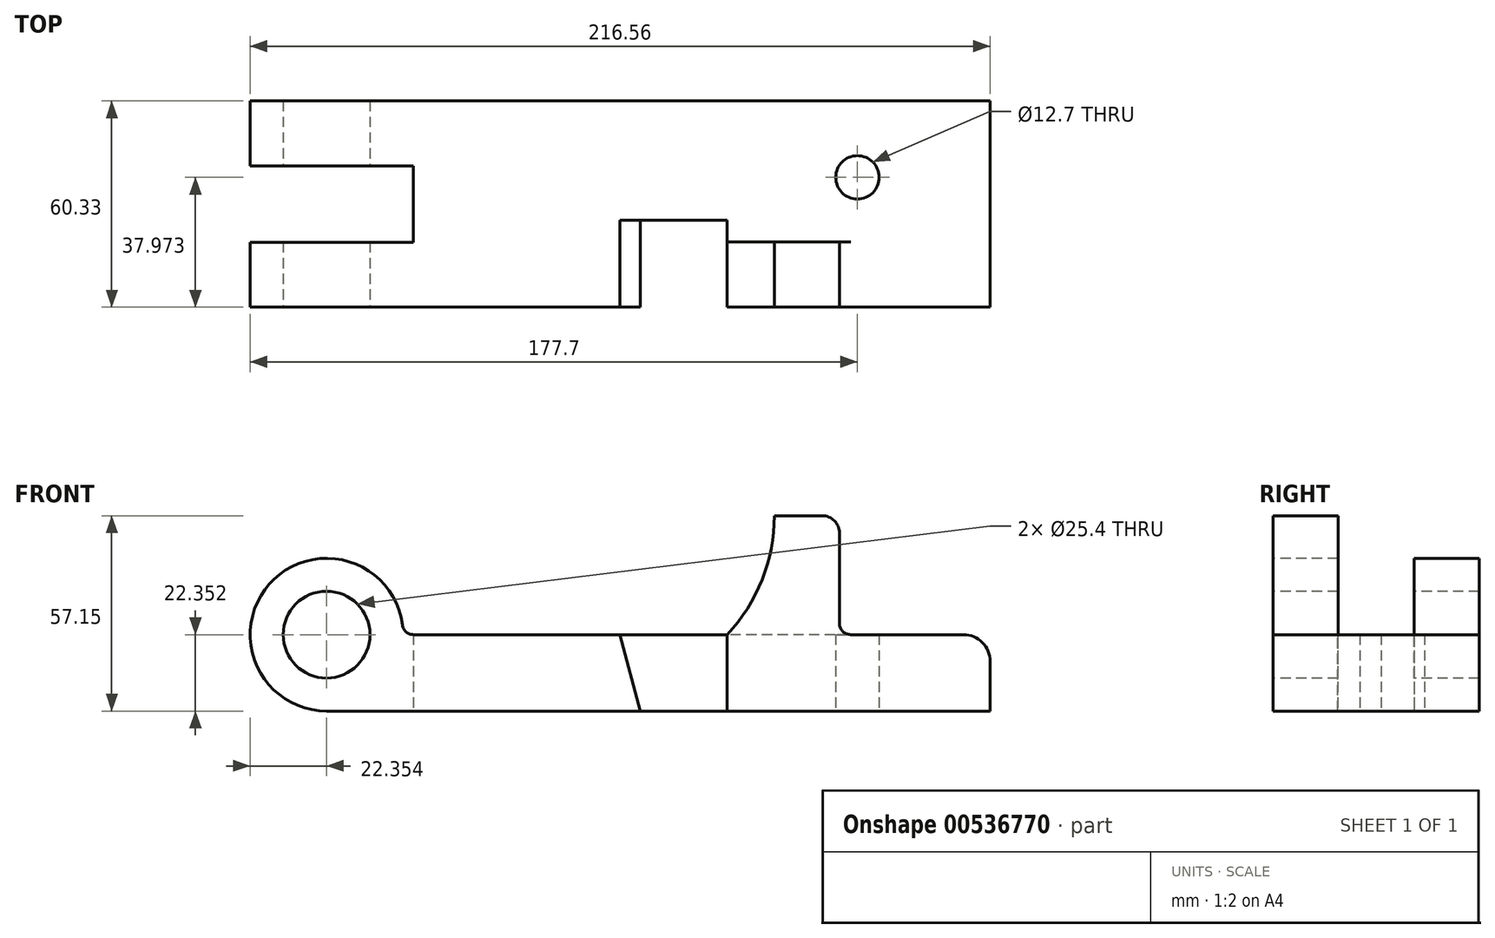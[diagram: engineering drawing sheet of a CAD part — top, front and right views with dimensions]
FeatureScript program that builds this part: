
annotation { "Feature Type Name" : "Feature", "Feature Type Description" : "" }
export const myFeature = defineFeature(function(context is Context, id is Id, definition is map)
    precondition{}
    {
        {
            var Q0;
            Q0=qCreatedBy(makeId("Front.planeOp"),FACE);
            var sketch = newSketch(context, id + "F0", { "sketchPlane" : qUnion([Q0])});
            skLineSegment(sketch, "E0", {"start": v(0, 0) * mm, "end": v(-91.85, 0) * mm});
            skLineSegment(sketch, "E1", {"start": v(0, 0) * mm, "end": v(102.36, 0) * mm});
            skLineSegment(sketch, "E2", {"start": v(102.36, 0) * mm, "end": v(102.36, 14.48) * mm});
            skLineSegment(sketch, "E3", {"start": v(61.54, 22.35) * mm, "end": v(94.49, 22.35) * mm});
            skLineSegment(sketch, "E4", {"start": v(58.24, 25.65) * mm, "end": v(58.24, 52.07) * mm});
            skLineSegment(sketch, "E5", {"start": v(53.16, 57.15) * mm, "end": v(39.2, 57.15) * mm});
            skLineSegment(sketch, "E6", {"start": v(39.2, 57.15) * mm, "end": v(39.2, 22.35) * mm, "construction": true});
            skLineSegment(sketch, "E7", {"start": v(39.2, 22.35) * mm, "end": v(25.4, 22.35) * mm});
            skLineSegment(sketch, "E8", {"start": v(25.4, 22.35) * mm, "end": v(-6, 22.35) * mm});
            skLineSegment(sketch, "E9", {"start": v(-6, 22.35) * mm, "end": v(-66.4, 22.35) * mm});
            skCircle(sketch, "E10", {"center": v(-91.85, 22.35) * mm, "radius": 12.7 * mm});
            skArc(sketch, "E11", {"start": v(102.36, 14.48) * mm, "mid": v(100.06, 20.05) * mm, "end": v(94.49, 22.35) * mm});
            skPoint(sketch, "E12", {"position": v(102.36, 22.35) * mm});
            skArc(sketch, "E13", {"start": v(-69.5, 22.35) * mm, "mid": v(-69.54, 23.8) * mm, "end": v(-69.68, 25.23) * mm, "construction": true});
            skArc(sketch, "E14", {"start": v(-91.85, 0) * mm, "mid": v(-76.04, 6.55) * mm, "end": v(-69.5, 22.35) * mm, "construction": true});
            skLineSegment(sketch, "E15", {"start": v(-6, 22.35) * mm, "end": v(0, 0) * mm});
            skLineSegment(sketch, "E16", {"start": v(25.4, 22.35) * mm, "end": v(25.4, 0) * mm});
            skArc(sketch, "E17", {"start": v(25.4, 22.35) * mm, "mid": v(35.62, 38.43) * mm, "end": v(39.2, 57.15) * mm});
            skArc(sketch, "E18", {"start": v(-69.68, 25.23) * mm, "mid": v(-68.59, 23.17) * mm, "end": v(-66.4, 22.35) * mm});
            skLineSegment(sketch, "E19", {"start": v(-66.4, 22.35) * mm, "end": v(-69.5, 22.35) * mm, "construction": true});
            skArc(sketch, "E20", {"start": v(-69.68, 25.23) * mm, "mid": v(-108.64, 37.1) * mm, "end": v(-91.85, 0) * mm});
            skArc(sketch, "E21", {"start": v(58.24, 52.07) * mm, "mid": v(56.75, 55.66) * mm, "end": v(53.16, 57.15) * mm});
            skArc(sketch, "E22", {"start": v(58.24, 25.65) * mm, "mid": v(59.2, 23.32) * mm, "end": v(61.54, 22.35) * mm});
            skPoint(sketch, "E23.orphan", {"position": v(58.24, 22.35) * mm});
            skPoint(sketch, "E24.orphan", {"position": v(58.24, 57.15) * mm});
            skLineSegment(sketch, "E25", {"start": v(61.54, 22.35) * mm, "end": v(58.24, 22.35) * mm});
            skLineSegment(sketch, "E26", {"start": v(58.24, 22.35) * mm, "end": v(39.2, 22.35) * mm});
            skSolve(sketch);
        }
        {
            var Q0;
            Q0=makeQuery(id+"F0.imprint","IMPRINT",FACE,{"disambiguationData":[TD([[makeQuery(id+"F0.imprint","IMPRINT",EDGE,{"derivedFrom":sQuery(id+"F0.wireOp",EDGE,"E0")}),-1.0]])]});
            var Q1;
            {var subQ0=sQuery(id+"F0.wireOp",EDGE,"E2");Q1=makeQuery(id+"F0.imprint","IMPRINT",FACE,{"disambiguationData":[TD([[makeQuery(id+"F0.imprint","IMPRINT",EDGE,{"derivedFrom":subQ0}),1.0]])]});}
            var Q2;
            Q2=makeQuery(id+"F0.imprint","IMPRINT",FACE,{"disambiguationData":[TD([[makeQuery(id+"F0.imprint","IMPRINT",EDGE,{"derivedFrom":sQuery(id+"F0.wireOp",EDGE,"E8")}),1.0]])]});
            extrude(context, id + "F1", {"entities" : qUnion([Q0, Q1, Q2]), "oppositeDirection" : true, "depth" : 60.32 * mm, "offsetDistance" : 25.4 * mm});
        }
        {
            var Q0;
            Q0=makeQuery(id+"F0.imprint","IMPRINT",FACE,{"disambiguationData":[TD([[makeQuery(id+"F0.imprint","IMPRINT",EDGE,{"derivedFrom":sQuery(id+"F0.wireOp",EDGE,"E4")}),1.0]])]});
            extrude(context, id + "F2", {"entities" : qUnion([Q0]), "operationType" : NewBodyOperationType.ADD, "oppositeDirection" : true, "depth" : 19.05 * mm, "offsetDistance" : 25.4 * mm});
        }
        {
            var Q0;
            Q0=makeQuery(id+"F0.imprint","IMPRINT",FACE,{"disambiguationData":[TD([[makeQuery(id+"F0.imprint","IMPRINT",EDGE,{"derivedFrom":sQuery(id+"F0.wireOp",EDGE,"E8")}),1.0]])]});
            extrude(context, id + "F3", {"entities" : qUnion([Q0]), "operationType" : NewBodyOperationType.REMOVE, "oppositeDirection" : true, "depth" : 19.05 * mm, "offsetDistance" : 25.4 * mm});
        }
        {
            var Q0;
            Q0=makeQuery(id+"F0.imprint","IMPRINT",FACE,{"disambiguationData":[TD([[makeQuery(id+"F0.imprint","IMPRINT",EDGE,{"derivedFrom":sQuery(id+"F0.wireOp",EDGE,"E8")}),1.0]])]});
            extrude(context, id + "F4", {"entities" : qUnion([Q0]), "operationType" : NewBodyOperationType.REMOVE, "oppositeDirection" : true, "depth" : 25.4 * mm, "offsetDistance" : 25.4 * mm});
        }
        {
            var Q0;
            Q0=qCreatedBy(makeId("Top.planeOp"),FACE);
            var sketch = newSketch(context, id + "F5", { "sketchPlane" : qUnion([Q0])});
            skLineSegment(sketch, "E27", {"start": v(102.36, 60.33) * mm, "end": v(102.36, 37.97) * mm, "construction": true});
            skLineSegment(sketch, "E28", {"start": v(102.36, 37.97) * mm, "end": v(63.5, 37.97) * mm, "construction": true});
            skCircle(sketch, "E29", {"center": v(63.5, 37.97) * mm, "radius": 6.35 * mm});
            skLineSegment(sketch, "E30", {"start": v(-91.85, 0) * mm, "end": v(-66.4, 0) * mm, "construction": true});
            skLineSegment(sketch, "E31", {"start": v(-91.85, 0) * mm, "end": v(-117.29, 0) * mm, "construction": true});
            skLineSegment(sketch, "E32", {"start": v(-66.4, 0) * mm, "end": v(-66.4, 19) * mm, "construction": true});
            skLineSegment(sketch, "E33", {"start": v(-66.4, 19) * mm, "end": v(-66.4, 41.33) * mm});
            skLineSegment(sketch, "E34", {"start": v(-66.4, 41.33) * mm, "end": v(-66.4, 60.33) * mm, "construction": true});
            skLineSegment(sketch, "E35", {"start": v(-117.29, 0) * mm, "end": v(-117.29, 60.33) * mm, "construction": true});
            skLineSegment(sketch, "E36", {"start": v(-117.29, 60.33) * mm, "end": v(-66.4, 60.33) * mm, "construction": true});
            skLineSegment(sketch, "E37", {"start": v(-66.4, 41.33) * mm, "end": v(-117.29, 41.33) * mm});
            skLineSegment(sketch, "E38", {"start": v(-117.29, 41.33) * mm, "end": v(-117.29, 19) * mm});
            skLineSegment(sketch, "E39", {"start": v(-117.29, 19) * mm, "end": v(-66.4, 19) * mm});
            skSolve(sketch);
        }
        {
            var Q0;
            Q0 = qSketchRegion(id + "F5", true);
            extrude(context, id + "F6", {"entities" : qUnion([Q0]), "operationType" : NewBodyOperationType.REMOVE, "endBound" : BoundingType.THROUGH_ALL, "depth" : 25.4 * mm, "offsetDistance" : 25.4 * mm});
        }
    });
